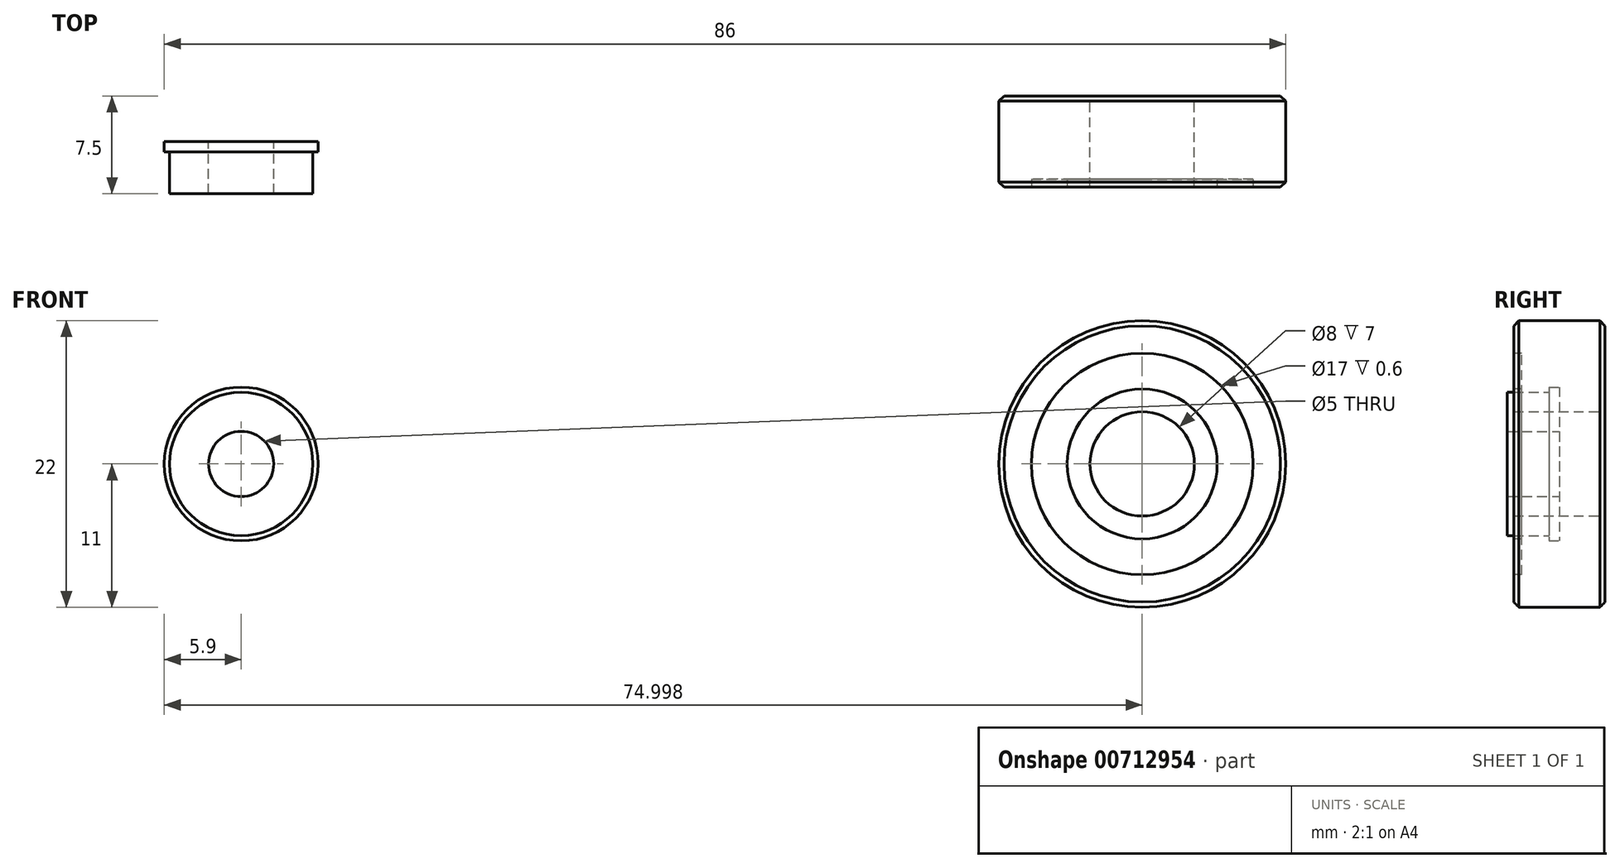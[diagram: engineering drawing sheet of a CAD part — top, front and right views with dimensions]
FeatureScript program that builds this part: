
annotation { "Feature Type Name" : "Feature", "Feature Type Description" : "" }
export const myFeature = defineFeature(function(context is Context, id is Id, definition is map)
    precondition{}
    {
        {
            var Q0;
            Q0=qCreatedBy(makeId("Right.planeOp"),FACE);
            var sketch = newSketch(context, id + "F0", { "sketchPlane" : qUnion([Q0])});
            skLineSegment(sketch, "E0", {"start": v(3.3, 0) * mm, "end": v(-12.28, 0) * mm, "construction": true});
            skLineSegment(sketch, "E1", {"start": v(0, 5.9) * mm, "end": v(-0.8, 5.9) * mm});
            skLineSegment(sketch, "E2", {"start": v(-0.8, 5.9) * mm, "end": v(-0.8, 5.5) * mm});
            skLineSegment(sketch, "E3", {"start": v(-0.8, 5.5) * mm, "end": v(-4, 5.5) * mm});
            skLineSegment(sketch, "E4", {"start": v(-4, 5.5) * mm, "end": v(-4, 2.5) * mm});
            skLineSegment(sketch, "E5", {"start": v(-4, 2.5) * mm, "end": v(0, 2.5) * mm});
            skLineSegment(sketch, "E6", {"start": v(0, 2.5) * mm, "end": v(0, 5.9) * mm});
            skSolve(sketch);
        }
        {
            var Q0;
            Q0=qSketchRegion(id+"F0",true);
            var Q1;
            Q1=sQuery(id+"F0.wireOp",EDGE,"E0");
            revolve(context, id + "F1", {"surfaceOperationType" : NewSurfaceOperationType.NEW, "entities" : qUnion([Q0]), "axis" : qUnion([Q1]), "revolveType" : RevolveType.FULL});
        }
        {
            var Q0;
            Q0=qCreatedBy(makeId("Front.planeOp"),FACE);
            var sketch = newSketch(context, id + "F2", { "sketchPlane" : qUnion([Q0])});
            skCircle(sketch, "E7", {"center": v(35.4, 0) * mm, "radius": 4 * mm});
            skCircle(sketch, "E8", {"center": v(35.4, 0) * mm, "radius": 11 * mm});
            skSolve(sketch);
        }
        {
            var Q0;
            Q0=makeQuery(id+"F1.opRevolve","SWEPT_BODY",BODY,{"disambiguationData":[OSD([sQuery(id+"F0.wireOp",EDGE,"E1"),sQuery(id+"F0.wireOp",EDGE,"E2"),sQuery(id+"F0.wireOp",EDGE,"E3"),sQuery(id+"F0.wireOp",EDGE,"E4"),sQuery(id+"F0.wireOp",EDGE,"E5"),sQuery(id+"F0.wireOp",EDGE,"E6")])]});
            transform(context, id + "F3", {"entities" : qUnion([Q0]), "transformType" : TransformType.TRANSLATION_3D, "dx" : -33.7 * mm, "dy" : 0 * mm, "dz" : 0 * mm, "makeCopy" : false});
        }
        {
            var Q0;
            Q0=makeQuery(id+"F2.imprint","IMPRINT",FACE,{"disambiguationData":[TD([[makeQuery(id+"F2.imprint","IMPRINT",EDGE,{"derivedFrom":sQuery(id+"F2.wireOp",EDGE,"E7")}),-1.0]])]});
            extrude(context, id + "F4", {"entities" : qUnion([Q0]), "depth" : 7 * mm, "offsetDistance" : 25 * mm, "symmetric" : true});
        }
        {
            var Q0;
            Q0=makeQuery(id+"F4.opExtrude","CAP_FACE",FACE,{"disambiguationData":[OSD([sQuery(id+"F2.wireOp",EDGE,"E7"),sQuery(id+"F2.wireOp",EDGE,"E8")])],"isStart":false});
            var sketch = newSketch(context, id + "F5", { "sketchPlane" : qUnion([Q0])});
            skCircle(sketch, "E9", {"center": v(35.4, 0) * mm, "radius": 5.75 * mm});
            skCircle(sketch, "E10", {"center": v(35.4, 0) * mm, "radius": 8.5 * mm});
            skSolve(sketch);
        }
        {
            var Q0;
            Q0=makeQuery(id+"F5.imprint","IMPRINT",FACE,{"disambiguationData":[TD([[makeQuery(id+"F5.imprint","IMPRINT",EDGE,{"derivedFrom":sQuery(id+"F5.wireOp",EDGE,"E9")}),-1.0]])]});
            extrude(context, id + "F6", {"entities" : qUnion([Q0]), "operationType" : NewBodyOperationType.REMOVE, "oppositeDirection" : true, "depth" : 0.6 * mm, "offsetDistance" : 25 * mm});
        }
        {
            var Q0;
            Q0=makeQuery(id+"F4.opExtrude","CAP_EDGE",EDGE,{"disambiguationData":[OSD([sQuery(id+"F2.wireOp",EDGE,"E8")])],"isStart":false});
            var Q1;
            Q1=makeQuery(id+"F6.boolean.opBoolean","COPY",EDGE,{"derivedFrom":makeQuery(id+"F6.opExtrude","CAP_EDGE",EDGE,{"disambiguationData":[OSD([sQuery(id+"F5.wireOp",EDGE,"E10")])],"isStart":true})});
            var Q2;
            Q2=makeQuery(id+"F6.boolean.opBoolean","COPY",EDGE,{"derivedFrom":makeQuery(id+"F6.opExtrude","CAP_EDGE",EDGE,{"disambiguationData":[OSD([sQuery(id+"F5.wireOp",EDGE,"E9")])],"isStart":true})});
            var Q3;
            Q3=makeQuery(id+"FAqd1R1ERXR4cZm_4.1.F6.boolean.opBoolean","COPY",EDGE,{"derivedFrom":makeQuery(id+"FAqd1R1ERXR4cZm_4.1.F6.opExtrude","CAP_EDGE",EDGE,{"disambiguationData":[OSD([sQuery(id+"F5.wireOp",EDGE,"E9")])],"isStart":true})});
            var Q4;
            Q4=makeQuery(id+"FAqd1R1ERXR4cZm_4.1.F6.boolean.opBoolean","COPY",EDGE,{"derivedFrom":makeQuery(id+"FAqd1R1ERXR4cZm_4.1.F6.opExtrude","CAP_EDGE",EDGE,{"disambiguationData":[OSD([sQuery(id+"F5.wireOp",EDGE,"E10")])],"isStart":true})});
            var Q5;
            Q5=makeQuery(id+"F4.opExtrude","CAP_EDGE",EDGE,{"disambiguationData":[OSD([sQuery(id+"F2.wireOp",EDGE,"E8")])],"isStart":true});
            chamfer(context, id + "F7", {"entities" : qUnion([Q0, Q1, Q2, Q3, Q4, Q5]), "width" : 0.4 * mm, "tangentPropagation" : true});
        }
    });
